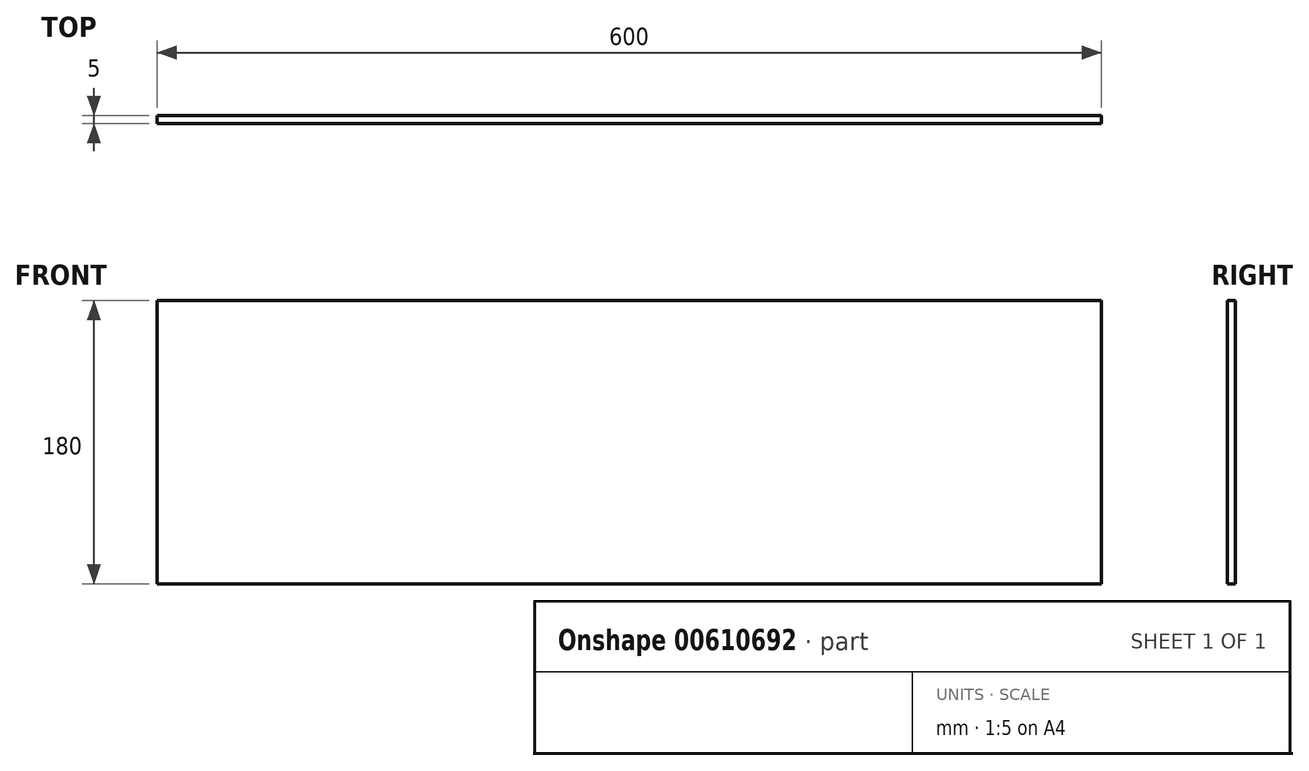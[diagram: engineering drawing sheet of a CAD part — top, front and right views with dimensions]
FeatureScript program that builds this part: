
annotation { "Feature Type Name" : "Feature", "Feature Type Description" : "" }
export const myFeature = defineFeature(function(context is Context, id is Id, definition is map)
    precondition{}
    {
        {
            var Q0;
            Q0=qCreatedBy(makeId("Front.planeOp"),FACE);
            var sketch = newSketch(context, id + "F0", { "sketchPlane" : qUnion([Q0])});
            skLineSegment(sketch, "E0.bottom", {"start": v(0, 0) * mm, "end": v(600, 0) * mm});
            skLineSegment(sketch, "E0.top", {"start": v(0, 180) * mm, "end": v(600, 180) * mm});
            skLineSegment(sketch, "E0.left", {"start": v(0, 0) * mm, "end": v(0, 180) * mm});
            skLineSegment(sketch, "E0.right", {"start": v(600, 0) * mm, "end": v(600, 180) * mm});
            skSolve(sketch);
        }
        {
            var Q0;
            Q0 = qSketchRegion(id + "F0", true);
            extrude(context, id + "F1", {"entities" : qUnion([Q0]), "depth" : 5 * mm, "offsetDistance" : 25 * mm});
        }
    });
